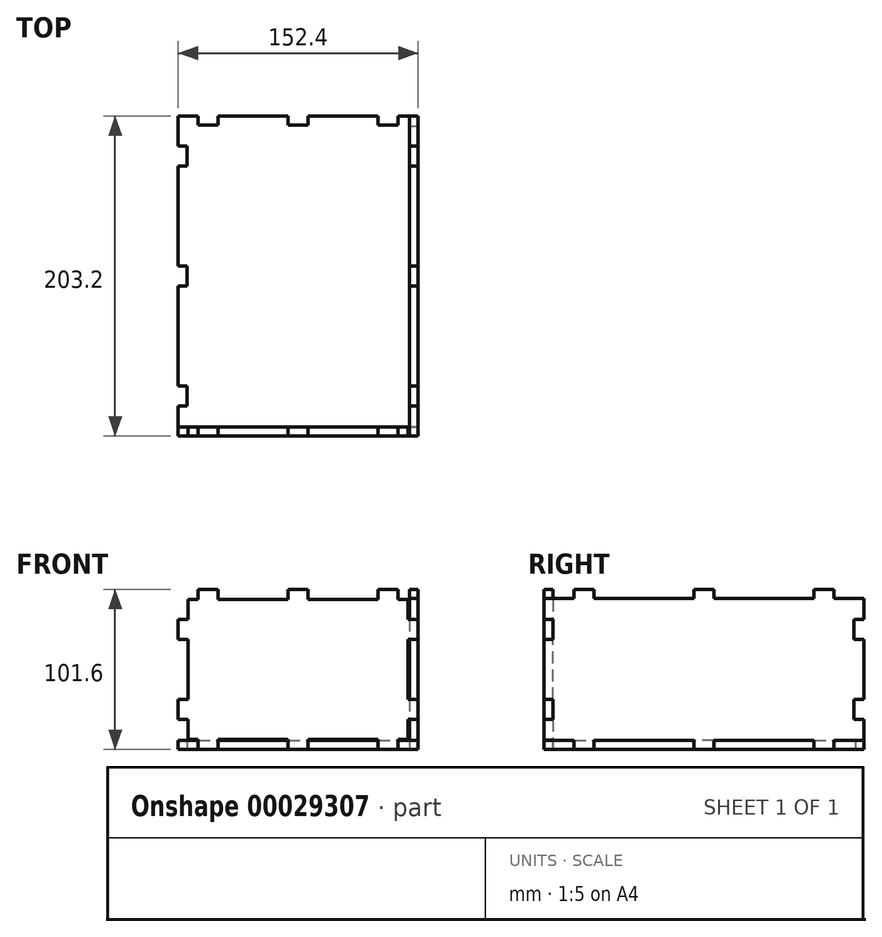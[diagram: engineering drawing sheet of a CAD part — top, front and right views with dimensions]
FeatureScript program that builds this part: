
annotation { "Feature Type Name" : "Feature", "Feature Type Description" : "" }
export const myFeature = defineFeature(function(context is Context, id is Id, definition is map)
    precondition{}
    {
        {
            var Q0;
            Q0=qCreatedBy(makeId("Top.planeOp"),FACE);
            var sketch = newSketch(context, id + "F0", { "sketchPlane" : qUnion([Q0])});
            skLineSegment(sketch, "E0", {"start": v(0, -101.6) * mm, "end": v(0, 101.6) * mm, "construction": true});
            skLineSegment(sketch, "E1", {"start": v(-76.2, 0) * mm, "end": v(76.2, 0) * mm, "construction": true});
            skLineSegment(sketch, "E2.0", {"start": v(38.1, -101.6) * mm, "end": v(38.1, 101.6) * mm, "construction": true});
            skLineSegment(sketch, "E3.0", {"start": v(76.2, -101.6) * mm, "end": v(76.2, -82.55) * mm, "construction": true});
            skLineSegment(sketch, "E4.0", {"start": v(-38.1, -101.6) * mm, "end": v(-38.1, 101.6) * mm, "construction": true});
            skLineSegment(sketch, "E5.0", {"start": v(-76.2, -101.6) * mm, "end": v(-76.2, 76.2) * mm, "construction": true});
            skLineSegment(sketch, "E6.0", {"start": v(-76.2, -50.8) * mm, "end": v(76.2, -50.8) * mm, "construction": true});
            skLineSegment(sketch, "E7.0", {"start": v(-76.2, -101.6) * mm, "end": v(-63.5, -101.6) * mm, "construction": true});
            skLineSegment(sketch, "E8.0", {"start": v(-76.2, 50.8) * mm, "end": v(76.2, 50.8) * mm, "construction": true});
            skLineSegment(sketch, "E9.0", {"start": v(-76.2, 101.6) * mm, "end": v(76.2, 101.6) * mm, "construction": true});
            skLineSegment(sketch, "E10.bottom", {"start": v(-76.2, -101.6) * mm, "end": v(-63.5, -101.6) * mm});
            skLineSegment(sketch, "E10.top", {"start": v(-76.2, 101.6) * mm, "end": v(-63.5, 101.6) * mm});
            skLineSegment(sketch, "E10.left", {"start": v(-76.2, -101.6) * mm, "end": v(-76.2, -82.55) * mm});
            skLineSegment(sketch, "E10.right", {"start": v(76.2, -101.6) * mm, "end": v(76.2, -82.55) * mm});
            skLineSegment(sketch, "E11.0", {"start": v(-57.15, -101.6) * mm, "end": v(-57.15, 101.6) * mm, "construction": true});
            skLineSegment(sketch, "E12.0", {"start": v(57.15, -101.6) * mm, "end": v(57.15, 101.6) * mm, "construction": true});
            skLineSegment(sketch, "E13.0", {"start": v(-76.2, -76.2) * mm, "end": v(76.2, -76.2) * mm, "construction": true});
            skLineSegment(sketch, "E14.0", {"start": v(-76.2, 76.2) * mm, "end": v(76.2, 76.2) * mm, "construction": true});
            skLineSegment(sketch, "E15.0", {"start": v(-76.2, -69.85) * mm, "end": v(76.2, -69.85) * mm, "construction": true});
            skLineSegment(sketch, "E16.0", {"start": v(-76.2, -82.55) * mm, "end": v(76.2, -82.55) * mm, "construction": true});
            skLineSegment(sketch, "E17.0", {"start": v(-70.61, -101.6) * mm, "end": v(-70.61, 101.6) * mm, "construction": true});
            skLineSegment(sketch, "E18.0", {"start": v(-76.2, -96.01) * mm, "end": v(76.2, -96.01) * mm, "construction": true});
            skLineSegment(sketch, "E19.0", {"start": v(-76.2, 96.01) * mm, "end": v(76.2, 96.01) * mm, "construction": true});
            skLineSegment(sketch, "E20.0", {"start": v(70.61, -101.6) * mm, "end": v(70.61, 101.6) * mm, "construction": true});
            skLineSegment(sketch, "E21", {"start": v(-76.2, -82.55) * mm, "end": v(-70.61, -82.55) * mm});
            skLineSegment(sketch, "E22", {"start": v(-70.61, -82.55) * mm, "end": v(-70.61, -69.85) * mm});
            skLineSegment(sketch, "E23", {"start": v(-70.61, -69.85) * mm, "end": v(-76.2, -69.85) * mm});
            skLineSegment(sketch, "E24", {"start": v(76.2, -82.55) * mm, "end": v(70.61, -82.55) * mm});
            skLineSegment(sketch, "E25", {"start": v(70.61, -82.55) * mm, "end": v(70.61, -69.85) * mm});
            skLineSegment(sketch, "E26", {"start": v(70.61, -69.85) * mm, "end": v(76.2, -69.85) * mm});
            skLineSegment(sketch, "E27.0", {"start": v(-76.2, 6.35) * mm, "end": v(76.2, 6.35) * mm, "construction": true});
            skLineSegment(sketch, "E28.0", {"start": v(-76.2, -6.35) * mm, "end": v(76.2, -6.35) * mm, "construction": true});
            skLineSegment(sketch, "E29", {"start": v(-76.2, -6.35) * mm, "end": v(-70.61, -6.35) * mm});
            skLineSegment(sketch, "E30.0", {"start": v(-76.2, 82.55) * mm, "end": v(76.2, 82.55) * mm, "construction": true});
            skLineSegment(sketch, "E31.0", {"start": v(-76.2, 69.85) * mm, "end": v(76.2, 69.85) * mm, "construction": true});
            skLineSegment(sketch, "E32", {"start": v(-70.61, -6.35) * mm, "end": v(-70.61, 6.35) * mm});
            skLineSegment(sketch, "E33", {"start": v(-70.61, 6.35) * mm, "end": v(-76.2, 6.35) * mm});
            skLineSegment(sketch, "E34", {"start": v(-76.2, 69.85) * mm, "end": v(-70.61, 69.85) * mm});
            skLineSegment(sketch, "E35", {"start": v(-70.61, 69.85) * mm, "end": v(-70.61, 82.55) * mm});
            skLineSegment(sketch, "E36", {"start": v(-70.61, 82.55) * mm, "end": v(-76.2, 82.55) * mm});
            skLineSegment(sketch, "E37", {"start": v(76.2, 69.85) * mm, "end": v(70.61, 69.85) * mm});
            skLineSegment(sketch, "E38", {"start": v(70.61, 69.85) * mm, "end": v(70.61, 82.55) * mm});
            skLineSegment(sketch, "E39", {"start": v(70.61, 82.55) * mm, "end": v(76.2, 82.55) * mm});
            skLineSegment(sketch, "E40", {"start": v(76.2, 6.35) * mm, "end": v(70.61, 6.35) * mm});
            skLineSegment(sketch, "E41", {"start": v(70.61, 6.35) * mm, "end": v(70.61, -6.35) * mm});
            skLineSegment(sketch, "E42", {"start": v(70.61, -6.35) * mm, "end": v(76.2, -6.35) * mm});
            skLineSegment(sketch, "E43.0", {"start": v(-63.5, -101.6) * mm, "end": v(-63.5, 101.6) * mm, "construction": true});
            skLineSegment(sketch, "E44.0", {"start": v(-50.8, -101.6) * mm, "end": v(-50.8, 101.6) * mm, "construction": true});
            skLineSegment(sketch, "E45.0", {"start": v(-6.35, -101.6) * mm, "end": v(-6.35, 101.6) * mm, "construction": true});
            skLineSegment(sketch, "E46.0", {"start": v(6.35, -101.6) * mm, "end": v(6.35, 101.6) * mm, "construction": true});
            skLineSegment(sketch, "E47.0", {"start": v(50.8, -101.6) * mm, "end": v(50.8, 101.6) * mm, "construction": true});
            skLineSegment(sketch, "E48.0", {"start": v(63.5, -101.6) * mm, "end": v(63.5, 101.6) * mm, "construction": true});
            skLineSegment(sketch, "E49", {"start": v(-63.5, -101.6) * mm, "end": v(-63.5, -96.01) * mm});
            skLineSegment(sketch, "E50", {"start": v(-63.5, -96.01) * mm, "end": v(-50.8, -96.01) * mm});
            skLineSegment(sketch, "E51", {"start": v(-50.8, -96.01) * mm, "end": v(-50.8, -101.6) * mm});
            skLineSegment(sketch, "E52", {"start": v(-6.35, -101.6) * mm, "end": v(-6.35, -96.01) * mm});
            skLineSegment(sketch, "E53", {"start": v(-6.35, -96.01) * mm, "end": v(6.35, -96.01) * mm});
            skLineSegment(sketch, "E54", {"start": v(6.35, -96.01) * mm, "end": v(6.35, -101.6) * mm});
            skLineSegment(sketch, "E55", {"start": v(50.8, -101.6) * mm, "end": v(50.8, -96.01) * mm});
            skLineSegment(sketch, "E56", {"start": v(50.8, -96.01) * mm, "end": v(63.5, -96.01) * mm});
            skLineSegment(sketch, "E57", {"start": v(63.5, -96.01) * mm, "end": v(63.5, -101.6) * mm});
            skLineSegment(sketch, "E58.trimOffspring", {"start": v(63.5, -101.6) * mm, "end": v(76.2, -101.6) * mm});
            skLineSegment(sketch, "E59.trimOffspring", {"start": v(76.2, -69.85) * mm, "end": v(76.2, -6.35) * mm});
            skLineSegment(sketch, "E60.trimOffspring", {"start": v(76.2, -69.85) * mm, "end": v(76.2, -6.35) * mm, "construction": true});
            skLineSegment(sketch, "E61.trimOffspring", {"start": v(76.2, 6.35) * mm, "end": v(76.2, 69.85) * mm});
            skLineSegment(sketch, "E62.trimOffspring", {"start": v(76.2, 6.35) * mm, "end": v(76.2, 69.85) * mm, "construction": true});
            skLineSegment(sketch, "E63.trimOffspring", {"start": v(76.2, 82.55) * mm, "end": v(76.2, 101.6) * mm});
            skLineSegment(sketch, "E64.trimOffspring", {"start": v(76.2, 82.55) * mm, "end": v(76.2, 101.6) * mm, "construction": true});
            skLineSegment(sketch, "E65.trimOffspring", {"start": v(-76.2, 82.55) * mm, "end": v(-76.2, 101.6) * mm});
            skLineSegment(sketch, "E66.trimOffspring", {"start": v(-76.2, 82.55) * mm, "end": v(-76.2, 101.6) * mm, "construction": true});
            skLineSegment(sketch, "E67.trimOffspring", {"start": v(-76.2, 6.35) * mm, "end": v(-76.2, 69.85) * mm});
            skLineSegment(sketch, "E68.trimOffspring", {"start": v(-76.2, -69.85) * mm, "end": v(-76.2, -6.35) * mm});
            skLineSegment(sketch, "E69.trimOffspring", {"start": v(-50.8, -101.6) * mm, "end": v(-6.35, -101.6) * mm});
            skLineSegment(sketch, "E70.trimOffspring", {"start": v(-57.15, -101.6) * mm, "end": v(76.2, -101.6) * mm, "construction": true});
            skLineSegment(sketch, "E71.trimOffspring", {"start": v(6.35, -101.6) * mm, "end": v(50.8, -101.6) * mm});
            skLineSegment(sketch, "E72", {"start": v(-63.5, 101.6) * mm, "end": v(-63.5, 96.01) * mm});
            skLineSegment(sketch, "E73", {"start": v(-63.5, 96.01) * mm, "end": v(-50.8, 96.01) * mm});
            skLineSegment(sketch, "E74", {"start": v(-50.8, 96.01) * mm, "end": v(-50.8, 101.6) * mm});
            skLineSegment(sketch, "E75", {"start": v(-6.35, 101.6) * mm, "end": v(-6.35, 96.01) * mm});
            skLineSegment(sketch, "E76", {"start": v(-6.35, 96.01) * mm, "end": v(6.35, 96.01) * mm});
            skLineSegment(sketch, "E77", {"start": v(6.35, 96.01) * mm, "end": v(6.35, 101.6) * mm});
            skLineSegment(sketch, "E78", {"start": v(50.8, 101.6) * mm, "end": v(50.8, 96.01) * mm});
            skLineSegment(sketch, "E79", {"start": v(50.8, 96.01) * mm, "end": v(63.5, 96.01) * mm});
            skLineSegment(sketch, "E80", {"start": v(63.5, 96.01) * mm, "end": v(63.5, 101.6) * mm});
            skLineSegment(sketch, "E81.trimOffspring", {"start": v(63.5, 101.6) * mm, "end": v(76.2, 101.6) * mm});
            skLineSegment(sketch, "E82.trimOffspring", {"start": v(6.35, 101.6) * mm, "end": v(50.8, 101.6) * mm});
            skLineSegment(sketch, "E83.trimOffspring", {"start": v(-50.8, 101.6) * mm, "end": v(-6.35, 101.6) * mm});
            skSolve(sketch);
        }
        {
            var Q0;
            Q0=makeQuery(id+"F0.imprint","IMPRINT",FACE,{"disambiguationData":[TD([[makeQuery(id+"F0.imprint","IMPRINT",EDGE,{"derivedFrom":sQuery(id+"F0.wireOp",EDGE,"E10.bottom")}),1.0]])]});
            extrude(context, id + "F1", {"entities" : qUnion([Q0]), "depth" : 5.6 * mm});
        }
        {
            var Q0;
            Q0=qCreatedBy(makeId("Right.planeOp"),FACE);
            cPlane(context, id + "F2", {"entities" : qUnion([Q0]), "cplaneType" : CPlaneType.OFFSET, "offset" : 76.2 * mm, "width" : 152.4 * mm, "height" : 152.4 * mm});
        }
        {
            var Q0;
            Q0=qCreatedBy(id+"F2.planeOp",FACE);
            var sketch = newSketch(context, id + "F3", { "sketchPlane" : qUnion([Q0])});
            skLineSegment(sketch, "E84", {"start": v(0, 0) * mm, "end": v(0, 101.6) * mm, "construction": true});
            skLineSegment(sketch, "E85", {"start": v(0, 50.8) * mm, "end": v(-101.6, 50.8) * mm, "construction": true});
            skLineSegment(sketch, "E86", {"start": v(0, 50.8) * mm, "end": v(101.6, 50.8) * mm, "construction": true});
            skPoint(sketch, "E87.0", {"position": v(-76.2, 0) * mm});
            skPoint(sketch, "E88.0", {"position": v(76.2, 0) * mm});
            skLineSegment(sketch, "E89.0", {"start": v(0, 101.6) * mm, "end": v(-101.6, 101.6) * mm, "construction": true});
            skLineSegment(sketch, "E90.0", {"start": v(0, 101.6) * mm, "end": v(101.6, 101.6) * mm, "construction": true});
            skLineSegment(sketch, "E91.0", {"start": v(101.6, 0) * mm, "end": v(101.6, 101.6) * mm, "construction": true});
            skLineSegment(sketch, "E92.0", {"start": v(-101.6, 0) * mm, "end": v(-101.6, 101.6) * mm, "construction": true});
            skLineSegment(sketch, "E93.0", {"start": v(0, 0) * mm, "end": v(-101.6, 0) * mm, "construction": true});
            skLineSegment(sketch, "E94.0", {"start": v(0, 0) * mm, "end": v(101.6, 0) * mm, "construction": true});
            skLineSegment(sketch, "E95.0", {"start": v(0, 25.4) * mm, "end": v(101.6, 25.4) * mm, "construction": true});
            skLineSegment(sketch, "E96.0", {"start": v(0, 76.2) * mm, "end": v(101.6, 76.2) * mm, "construction": true});
            skLineSegment(sketch, "E97.0", {"start": v(0, 76.2) * mm, "end": v(-101.6, 76.2) * mm, "construction": true});
            skLineSegment(sketch, "E98.0", {"start": v(0, 25.4) * mm, "end": v(-101.6, 25.4) * mm, "construction": true});
            skLineSegment(sketch, "E99.0", {"start": v(-101.6, 5.59) * mm, "end": v(-82.55, 5.59) * mm});
            skLineSegment(sketch, "E100.0", {"start": v(-82.55, 5.59) * mm, "end": v(-82.55, 0) * mm});
            skLineSegment(sketch, "E101.0", {"start": v(-69.85, 5.59) * mm, "end": v(-69.85, 0) * mm});
            skLineSegment(sketch, "E102.0", {"start": v(-69.85, 5.59) * mm, "end": v(-6.35, 5.59) * mm});
            skLineSegment(sketch, "E103.0", {"start": v(-6.35, 5.59) * mm, "end": v(-6.35, 0) * mm});
            skLineSegment(sketch, "E104.0", {"start": v(6.35, 5.59) * mm, "end": v(6.35, 0) * mm});
            skLineSegment(sketch, "E105.0", {"start": v(6.35, 5.59) * mm, "end": v(69.85, 5.59) * mm});
            skLineSegment(sketch, "E106.0", {"start": v(69.85, 5.59) * mm, "end": v(69.85, 0) * mm});
            skLineSegment(sketch, "E107.0", {"start": v(82.55, 5.59) * mm, "end": v(82.55, 0) * mm});
            skLineSegment(sketch, "E108.0", {"start": v(82.55, 5.59) * mm, "end": v(101.6, 5.59) * mm});
            skLineSegment(sketch, "E109.MirrorCS", {"start": v(-101.6, 96.01) * mm, "end": v(-82.55, 96.01) * mm});
            skLineSegment(sketch, "E110.MirrorCS", {"start": v(-82.55, 96.01) * mm, "end": v(-82.55, 101.6) * mm});
            skLineSegment(sketch, "E111.MirrorCS", {"start": v(-69.85, 96.01) * mm, "end": v(-69.85, 101.6) * mm});
            skLineSegment(sketch, "E112.MirrorCS", {"start": v(-69.85, 96.01) * mm, "end": v(-6.35, 96.01) * mm});
            skLineSegment(sketch, "E113.MirrorCS", {"start": v(-6.35, 96.01) * mm, "end": v(-6.35, 101.6) * mm});
            skLineSegment(sketch, "E114.MirrorCS", {"start": v(6.35, 96.01) * mm, "end": v(6.35, 101.6) * mm});
            skLineSegment(sketch, "E115.MirrorCS", {"start": v(6.35, 96.01) * mm, "end": v(69.85, 96.01) * mm});
            skLineSegment(sketch, "E116.MirrorCS", {"start": v(69.85, 96.01) * mm, "end": v(69.85, 101.6) * mm});
            skLineSegment(sketch, "E117.MirrorCS", {"start": v(82.55, 96.01) * mm, "end": v(82.55, 101.6) * mm});
            skLineSegment(sketch, "E118.MirrorCS", {"start": v(82.55, 96.01) * mm, "end": v(101.6, 96.01) * mm});
            skLineSegment(sketch, "E119", {"start": v(-76.2, 0) * mm, "end": v(-76.2, 101.6) * mm, "construction": true});
            skLineSegment(sketch, "E120", {"start": v(76.2, 0) * mm, "end": v(76.2, 101.6) * mm, "construction": true});
            skLineSegment(sketch, "E121", {"start": v(-82.55, 101.6) * mm, "end": v(-69.85, 101.6) * mm});
            skLineSegment(sketch, "E122", {"start": v(-6.35, 101.6) * mm, "end": v(6.35, 101.6) * mm});
            skLineSegment(sketch, "E123", {"start": v(69.85, 101.6) * mm, "end": v(82.55, 101.6) * mm});
            skLineSegment(sketch, "E124.0", {"start": v(0, 31.75) * mm, "end": v(-101.6, 31.75) * mm, "construction": true});
            skLineSegment(sketch, "E125.0", {"start": v(0, 19.05) * mm, "end": v(-101.6, 19.05) * mm, "construction": true});
            skLineSegment(sketch, "E126.0", {"start": v(-96.01, 0) * mm, "end": v(-96.01, 101.6) * mm, "construction": true});
            skLineSegment(sketch, "E127.0", {"start": v(95.25, 0) * mm, "end": v(95.25, 101.6) * mm, "construction": true});
            skLineSegment(sketch, "E128.0", {"start": v(0, 69.85) * mm, "end": v(-101.6, 69.85) * mm, "construction": true});
            skLineSegment(sketch, "E129.0", {"start": v(0, 82.55) * mm, "end": v(-101.6, 82.55) * mm, "construction": true});
            skLineSegment(sketch, "E130.0", {"start": v(0, 82.55) * mm, "end": v(101.6, 82.55) * mm, "construction": true});
            skLineSegment(sketch, "E131.0", {"start": v(0, 69.85) * mm, "end": v(101.6, 69.85) * mm, "construction": true});
            skLineSegment(sketch, "E132.0", {"start": v(0, 19.05) * mm, "end": v(101.6, 19.05) * mm, "construction": true});
            skLineSegment(sketch, "E133.0", {"start": v(0, 31.75) * mm, "end": v(101.6, 31.75) * mm, "construction": true});
            skLineSegment(sketch, "E134", {"start": v(-101.6, 96.01) * mm, "end": v(-101.6, 82.55) * mm});
            skLineSegment(sketch, "E135", {"start": v(-101.6, 82.55) * mm, "end": v(-96.01, 82.55) * mm});
            skLineSegment(sketch, "E136", {"start": v(-96.01, 82.55) * mm, "end": v(-96.01, 69.85) * mm});
            skLineSegment(sketch, "E137", {"start": v(-96.01, 69.85) * mm, "end": v(-101.6, 69.85) * mm});
            skLineSegment(sketch, "E138", {"start": v(-101.6, 69.85) * mm, "end": v(-101.6, 31.75) * mm});
            skLineSegment(sketch, "E139", {"start": v(-101.6, 31.75) * mm, "end": v(-96.01, 31.75) * mm});
            skLineSegment(sketch, "E140", {"start": v(-96.01, 31.75) * mm, "end": v(-96.01, 19.05) * mm});
            skLineSegment(sketch, "E141", {"start": v(-96.01, 19.05) * mm, "end": v(-101.6, 19.05) * mm});
            skLineSegment(sketch, "E142", {"start": v(-101.6, 19.05) * mm, "end": v(-101.6, 5.59) * mm});
            skLineSegment(sketch, "E143", {"start": v(101.6, 5.59) * mm, "end": v(101.6, 19.05) * mm});
            skLineSegment(sketch, "E144", {"start": v(95.25, 19.05) * mm, "end": v(95.25, 31.75) * mm});
            skLineSegment(sketch, "E145", {"start": v(95.25, 31.75) * mm, "end": v(101.6, 31.75) * mm});
            skLineSegment(sketch, "E146", {"start": v(101.6, 31.75) * mm, "end": v(101.6, 69.85) * mm});
            skLineSegment(sketch, "E147", {"start": v(95.25, 69.85) * mm, "end": v(95.25, 82.55) * mm});
            skLineSegment(sketch, "E148", {"start": v(95.25, 82.55) * mm, "end": v(101.6, 82.55) * mm});
            skLineSegment(sketch, "E149", {"start": v(101.6, 82.55) * mm, "end": v(101.6, 96.01) * mm});
            skLineSegment(sketch, "E150", {"start": v(101.6, 69.85) * mm, "end": v(95.25, 69.85) * mm});
            skLineSegment(sketch, "E151", {"start": v(101.6, 19.05) * mm, "end": v(95.25, 19.05) * mm});
            skLineSegment(sketch, "E152", {"start": v(-82.55, 0) * mm, "end": v(-69.85, 0) * mm});
            skLineSegment(sketch, "E153", {"start": v(-6.35, 0) * mm, "end": v(6.35, 0) * mm});
            skLineSegment(sketch, "E154", {"start": v(69.85, 0) * mm, "end": v(82.55, 0) * mm});
            skSolve(sketch);
        }
        {
            var Q0;
            Q0=makeQuery(id+"F3.imprint","IMPRINT",FACE,{"disambiguationData":[TD([[makeQuery(id+"F3.imprint","IMPRINT",EDGE,{"derivedFrom":sQuery(id+"F3.wireOp",EDGE,"E99.0")}),1.0]])]});
            extrude(context, id + "F4", {"entities" : qUnion([Q0]), "oppositeDirection" : true, "depth" : 5.6 * mm});
        }
        {
            var Q0;
            Q0=makeQuery(id+"F1.opExtrude","SWEPT_FACE",FACE,{"disambiguationData":[OSD([sQuery(id+"F0.wireOp",EDGE,"E69.trimOffspring")])]});
            var Q1;
            Q1=makeQuery(id+"F1.opExtrude","CAP_VERTEX",VERTEX,{"disambiguationData":[OSD([sQuery(id+"F0.wireOp",EDGE,"E52"),sQuery(id+"F0.wireOp",EDGE,"E69.trimOffspring")])],"isStart":false});
            cPlane(context, id + "F5", {"entities" : qUnion([Q0, Q1]), "cplaneType" : CPlaneType.PLANE_POINT, "offset" : 152.4 * mm, "width" : 152.4 * mm, "height" : 152.4 * mm});
        }
        {
            var Q0;
            Q0=qCreatedBy(id+"F5.planeOp",FACE);
            var sketch = newSketch(context, id + "F6", { "sketchPlane" : qUnion([Q0])});
            skLineSegment(sketch, "E155", {"start": v(0, 0) * mm, "end": v(0, 50.8) * mm, "construction": true});
            skLineSegment(sketch, "E156.0", {"start": v(76.2, 69.85) * mm, "end": v(76.2, 31.75) * mm, "construction": true});
            skLineSegment(sketch, "E157", {"start": v(76.2, 50.8) * mm, "end": v(0, 50.8) * mm, "construction": true});
            skLineSegment(sketch, "E158", {"start": v(0, 50.8) * mm, "end": v(-76.2, 50.8) * mm, "construction": true});
            skLineSegment(sketch, "E159", {"start": v(0, 50.8) * mm, "end": v(0, 101.6) * mm, "construction": true});
            skLineSegment(sketch, "E160.0", {"start": v(0, 25.4) * mm, "end": v(-76.2, 25.4) * mm, "construction": true});
            skLineSegment(sketch, "E161.0", {"start": v(0, 0) * mm, "end": v(-76.2, 0) * mm, "construction": true});
            skLineSegment(sketch, "E162.0", {"start": v(0, 76.2) * mm, "end": v(-76.2, 76.2) * mm, "construction": true});
            skLineSegment(sketch, "E163.0", {"start": v(0, 101.6) * mm, "end": v(-76.2, 101.6) * mm, "construction": true});
            skLineSegment(sketch, "E164", {"start": v(-76.2, 101.6) * mm, "end": v(-76.2, 0) * mm, "construction": true});
            skLineSegment(sketch, "E165.0", {"start": v(76.2, 76.2) * mm, "end": v(0, 76.2) * mm, "construction": true});
            skLineSegment(sketch, "E166.0", {"start": v(76.2, 101.6) * mm, "end": v(0, 101.6) * mm, "construction": true});
            skLineSegment(sketch, "E167.0", {"start": v(76.2, 25.4) * mm, "end": v(0, 25.4) * mm, "construction": true});
            skLineSegment(sketch, "E168.0", {"start": v(76.2, 0) * mm, "end": v(0, 0) * mm, "construction": true});
            skLineSegment(sketch, "E169.0", {"start": v(57.15, 0) * mm, "end": v(57.15, 50.8) * mm, "construction": true});
            skLineSegment(sketch, "E170.0", {"start": v(-57.15, 0) * mm, "end": v(-57.15, 50.8) * mm, "construction": true});
            skLineSegment(sketch, "E171", {"start": v(-57.15, 50.8) * mm, "end": v(-57.15, 101.6) * mm, "construction": true});
            skLineSegment(sketch, "E172", {"start": v(57.15, 50.8) * mm, "end": v(57.15, 101.6) * mm, "construction": true});
            skLineSegment(sketch, "E173.0", {"start": v(0, 69.85) * mm, "end": v(-76.2, 69.85) * mm, "construction": true});
            skLineSegment(sketch, "E174.0", {"start": v(0, 82.55) * mm, "end": v(-76.2, 82.55) * mm, "construction": true});
            skLineSegment(sketch, "E175.0", {"start": v(76.2, 69.85) * mm, "end": v(0, 69.85) * mm, "construction": true});
            skLineSegment(sketch, "E176.0", {"start": v(76.2, 82.55) * mm, "end": v(0, 82.55) * mm, "construction": true});
            skLineSegment(sketch, "E177.0", {"start": v(76.2, 19.05) * mm, "end": v(0, 19.05) * mm, "construction": true});
            skLineSegment(sketch, "E178.0", {"start": v(76.2, 31.75) * mm, "end": v(0, 31.75) * mm, "construction": true});
            skLineSegment(sketch, "E179.0", {"start": v(0, 19.05) * mm, "end": v(-76.2, 19.05) * mm, "construction": true});
            skLineSegment(sketch, "E180.0", {"start": v(0, 31.75) * mm, "end": v(-76.2, 31.75) * mm, "construction": true});
            skLineSegment(sketch, "E181.0", {"start": v(-63.5, 50.8) * mm, "end": v(-63.5, 101.6) * mm, "construction": true});
            skLineSegment(sketch, "E182.0", {"start": v(-50.8, 50.8) * mm, "end": v(-50.8, 101.6) * mm, "construction": true});
            skLineSegment(sketch, "E183.0", {"start": v(-63.5, 0) * mm, "end": v(-63.5, 50.8) * mm, "construction": true});
            skLineSegment(sketch, "E184.0", {"start": v(-50.8, 0) * mm, "end": v(-50.8, 50.8) * mm, "construction": true});
            skLineSegment(sketch, "E185.0", {"start": v(50.8, 50.8) * mm, "end": v(50.8, 101.6) * mm, "construction": true});
            skLineSegment(sketch, "E186.0", {"start": v(63.5, 50.8) * mm, "end": v(63.5, 101.6) * mm, "construction": true});
            skLineSegment(sketch, "E187.0", {"start": v(50.8, 0) * mm, "end": v(50.8, 50.8) * mm, "construction": true});
            skLineSegment(sketch, "E188.0", {"start": v(63.5, 0) * mm, "end": v(63.5, 50.8) * mm, "construction": true});
            skLineSegment(sketch, "E189.0", {"start": v(-6.35, 50.8) * mm, "end": v(-6.35, 101.6) * mm, "construction": true});
            skLineSegment(sketch, "E190.0", {"start": v(6.35, 50.8) * mm, "end": v(6.35, 101.6) * mm, "construction": true});
            skLineSegment(sketch, "E191.0", {"start": v(-6.35, 0) * mm, "end": v(-6.35, 50.8) * mm, "construction": true});
            skLineSegment(sketch, "E192.0", {"start": v(6.35, 0) * mm, "end": v(6.35, 50.8) * mm, "construction": true});
            skLineSegment(sketch, "E193.0", {"start": v(0, 95.25) * mm, "end": v(-69.85, 95.25) * mm, "construction": true});
            skLineSegment(sketch, "E193.1", {"start": v(69.85, 95.25) * mm, "end": v(0, 95.25) * mm, "construction": true});
            skLineSegment(sketch, "E193.3", {"start": v(69.85, 6.35) * mm, "end": v(0, 6.35) * mm, "construction": true});
            skLineSegment(sketch, "E193.4", {"start": v(0, 6.35) * mm, "end": v(-69.85, 6.35) * mm, "construction": true});
            skLineSegment(sketch, "E193.5", {"start": v(-69.85, 95.25) * mm, "end": v(-69.85, 6.35) * mm, "construction": true});
            skPoint(sketch, "E194.0", {"position": v(76.2, 101.6) * mm});
            skPoint(sketch, "E195.0", {"position": v(76.2, 0) * mm});
            skLineSegment(sketch, "E196", {"start": v(76.2, 101.6) * mm, "end": v(76.2, 0) * mm, "construction": true});
            skLineSegment(sketch, "E197.0", {"start": v(69.85, 101.6) * mm, "end": v(69.85, 0) * mm, "construction": true});
            skLineSegment(sketch, "E198", {"start": v(-76.2, 82.55) * mm, "end": v(-69.85, 82.55) * mm});
            skLineSegment(sketch, "E199", {"start": v(-69.85, 82.55) * mm, "end": v(-69.85, 95.25) * mm});
            skLineSegment(sketch, "E200", {"start": v(-63.5, 95.25) * mm, "end": v(-63.5, 101.6) * mm});
            skLineSegment(sketch, "E201", {"start": v(-50.8, 101.6) * mm, "end": v(-63.5, 101.6) * mm});
            skLineSegment(sketch, "E202", {"start": v(-63.5, 95.25) * mm, "end": v(-69.85, 95.25) * mm});
            skLineSegment(sketch, "E203", {"start": v(-50.8, 95.25) * mm, "end": v(-6.35, 95.25) * mm});
            skLineSegment(sketch, "E204", {"start": v(-6.35, 101.6) * mm, "end": v(6.35, 101.6) * mm});
            skLineSegment(sketch, "E205", {"start": v(6.35, 101.6) * mm, "end": v(6.35, 95.25) * mm});
            skLineSegment(sketch, "E206", {"start": v(6.35, 95.25) * mm, "end": v(50.8, 95.25) * mm});
            skLineSegment(sketch, "E207", {"start": v(50.8, 101.6) * mm, "end": v(63.5, 101.6) * mm});
            skLineSegment(sketch, "E208", {"start": v(63.5, 95.25) * mm, "end": v(69.85, 95.25) * mm});
            skLineSegment(sketch, "E209", {"start": v(69.85, 95.25) * mm, "end": v(69.85, 82.55) * mm});
            skLineSegment(sketch, "E210", {"start": v(69.85, 82.55) * mm, "end": v(76.2, 82.55) * mm});
            skLineSegment(sketch, "E211", {"start": v(76.2, 82.55) * mm, "end": v(76.2, 69.85) * mm});
            skLineSegment(sketch, "E212", {"start": v(76.2, 69.85) * mm, "end": v(69.85, 69.85) * mm});
            skLineSegment(sketch, "E213", {"start": v(69.85, 69.85) * mm, "end": v(69.85, 31.75) * mm});
            skLineSegment(sketch, "E214", {"start": v(69.85, 31.75) * mm, "end": v(76.2, 31.75) * mm});
            skLineSegment(sketch, "E215", {"start": v(76.2, 31.75) * mm, "end": v(76.2, 19.05) * mm});
            skLineSegment(sketch, "E216", {"start": v(76.2, 19.05) * mm, "end": v(69.85, 19.05) * mm});
            skLineSegment(sketch, "E217", {"start": v(69.85, 19.05) * mm, "end": v(69.85, 6.35) * mm});
            skLineSegment(sketch, "E218", {"start": v(69.85, 6.35) * mm, "end": v(63.5, 6.35) * mm});
            skLineSegment(sketch, "E219", {"start": v(63.5, 6.35) * mm, "end": v(63.5, 0) * mm});
            skLineSegment(sketch, "E220", {"start": v(63.5, 0) * mm, "end": v(50.8, 0) * mm});
            skLineSegment(sketch, "E221", {"start": v(50.8, 0) * mm, "end": v(50.8, 6.35) * mm});
            skLineSegment(sketch, "E222", {"start": v(50.8, 6.35) * mm, "end": v(6.35, 6.35) * mm});
            skLineSegment(sketch, "E223", {"start": v(6.35, 6.35) * mm, "end": v(6.35, 0) * mm});
            skLineSegment(sketch, "E224", {"start": v(6.35, 0) * mm, "end": v(-6.35, 0) * mm});
            skLineSegment(sketch, "E225", {"start": v(-6.35, 0) * mm, "end": v(-6.35, 6.35) * mm});
            skLineSegment(sketch, "E226", {"start": v(-6.35, 6.35) * mm, "end": v(-50.8, 6.35) * mm});
            skLineSegment(sketch, "E227", {"start": v(-50.8, 6.35) * mm, "end": v(-50.8, 0) * mm});
            skLineSegment(sketch, "E228", {"start": v(-50.8, 0) * mm, "end": v(-63.5, 0) * mm});
            skLineSegment(sketch, "E229", {"start": v(-63.5, 0) * mm, "end": v(-63.5, 6.35) * mm});
            skLineSegment(sketch, "E230", {"start": v(-63.5, 6.35) * mm, "end": v(-69.85, 6.35) * mm});
            skLineSegment(sketch, "E231", {"start": v(-69.85, 19.05) * mm, "end": v(-76.2, 19.05) * mm});
            skLineSegment(sketch, "E232", {"start": v(-76.2, 19.05) * mm, "end": v(-76.2, 31.75) * mm});
            skLineSegment(sketch, "E233", {"start": v(-76.2, 31.75) * mm, "end": v(-69.85, 31.75) * mm});
            skLineSegment(sketch, "E234", {"start": v(-69.85, 31.75) * mm, "end": v(-69.85, 69.85) * mm});
            skLineSegment(sketch, "E235", {"start": v(-69.85, 69.85) * mm, "end": v(-76.2, 69.85) * mm});
            skLineSegment(sketch, "E236", {"start": v(-76.2, 69.85) * mm, "end": v(-76.2, 82.55) * mm});
            skLineSegment(sketch, "E237", {"start": v(-6.35, 101.6) * mm, "end": v(-6.35, 95.25) * mm});
            skLineSegment(sketch, "E238", {"start": v(50.8, 101.6) * mm, "end": v(50.8, 95.25) * mm});
            skLineSegment(sketch, "E239", {"start": v(63.5, 101.6) * mm, "end": v(63.5, 95.25) * mm});
            skLineSegment(sketch, "E240", {"start": v(-50.8, 101.6) * mm, "end": v(-50.8, 95.25) * mm});
            skLineSegment(sketch, "E241", {"start": v(-69.85, 19.05) * mm, "end": v(-69.85, 6.35) * mm});
            skSolve(sketch);
        }
        {
            var Q0;
            Q0=makeQuery(id+"F6.imprint","IMPRINT",FACE,{"disambiguationData":[TD([[makeQuery(id+"F6.imprint","IMPRINT",EDGE,{"derivedFrom":sQuery(id+"F6.wireOp",EDGE,"E198")}),-1.0]])]});
            extrude(context, id + "F7", {"entities" : qUnion([Q0]), "oppositeDirection" : true, "depth" : 5.6 * mm});
        }
    });
